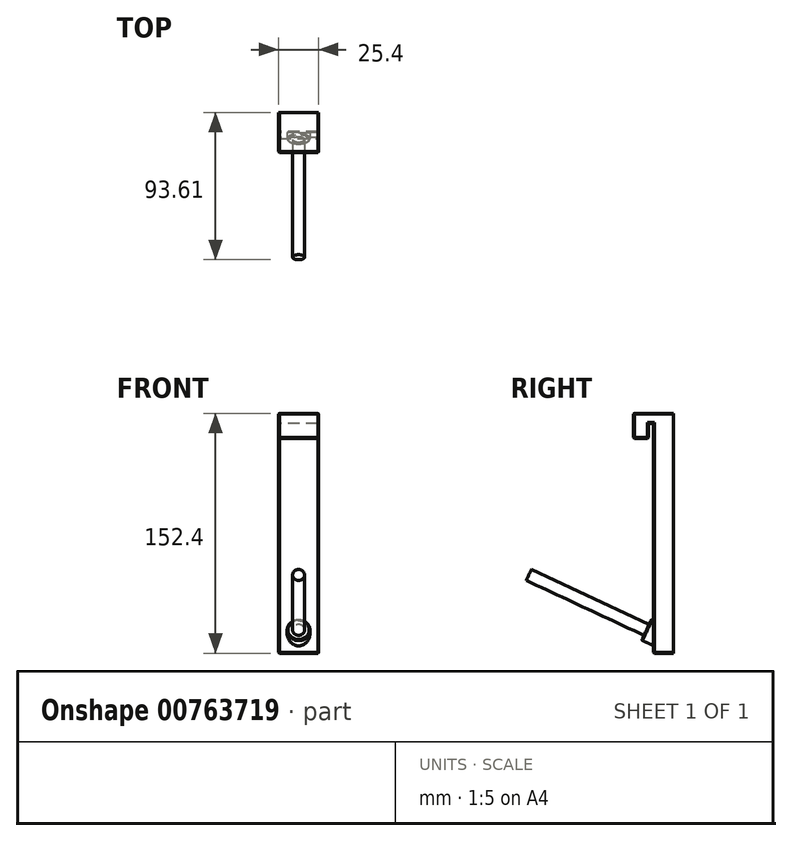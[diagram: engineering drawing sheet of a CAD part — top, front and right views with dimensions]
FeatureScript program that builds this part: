
annotation { "Feature Type Name" : "Feature", "Feature Type Description" : "" }
export const myFeature = defineFeature(function(context is Context, id is Id, definition is map)
    precondition{}
    {
        {
            var Q0;
            Q0=qCreatedBy(makeId("Right.planeOp"),FACE);
            var sketch = newSketch(context, id + "F0", { "sketchPlane" : qUnion([Q0])});
            skLineSegment(sketch, "E0.bottom", {"start": v(-12.7, 76.2) * mm, "end": v(12.7, 76.2) * mm});
            skLineSegment(sketch, "E0.top", {"start": v(-12.7, -76.2) * mm, "end": v(12.7, -76.2) * mm, "construction": true});
            skLineSegment(sketch, "E0.left", {"start": v(-12.7, 76.2) * mm, "end": v(-12.7, -76.2) * mm, "construction": true});
            skLineSegment(sketch, "E0.right", {"start": v(12.7, 76.2) * mm, "end": v(12.7, -76.2) * mm});
            skPoint(sketch, "E0.middle", {"position": v(0, 0) * mm});
            skLineSegment(sketch, "E1", {"start": v(-12.7, 76.2) * mm, "end": v(-12.7, 60.33) * mm});
            skLineSegment(sketch, "E2", {"start": v(-12.7, 60.33) * mm, "end": v(-3.3, 60.33) * mm});
            skLineSegment(sketch, "E3", {"start": v(-3.3, 60.33) * mm, "end": v(-3.3, 69.85) * mm});
            skLineSegment(sketch, "E4", {"start": v(-3.3, 69.85) * mm, "end": v(0, 69.85) * mm});
            skLineSegment(sketch, "E5", {"start": v(0, 69.85) * mm, "end": v(0, -76.2) * mm});
            skLineSegment(sketch, "E6", {"start": v(0, -76.2) * mm, "end": v(12.7, -76.2) * mm});
            skSolve(sketch);
        }
        {
            var Q0;
            Q0 = qSketchRegion(id + "F0", true);
            extrude(context, id + "F1", {"entities" : qUnion([Q0]), "endBound" : BoundingType.SYMMETRIC, "depth" : 25.4 * mm, "offsetDistance" : 25.4 * mm});
        }
        {
            var Q0;
            Q0=qCreatedBy(makeId("Right.planeOp"),FACE);
            var sketch = newSketch(context, id + "F2", { "sketchPlane" : qUnion([Q0])});
            skLineSegment(sketch, "E7", {"start": v(-79.3, -63.5) * mm, "end": v(-79.3, -26.52) * mm, "construction": true});
            skLineSegment(sketch, "E8", {"start": v(12.7, -63.5) * mm, "end": v(-79.3, -63.5) * mm, "construction": true});
            skLineSegment(sketch, "E9", {"start": v(0, 0) * mm, "end": v(0, -63.5) * mm, "construction": true});
            skLineSegment(sketch, "E10", {"start": v(-79.3, -26.52) * mm, "end": v(0, -63.5) * mm, "construction": true});
            skLineSegment(sketch, "E11", {"start": v(-79.3, -26.52) * mm, "end": v(-77.7, -23.07) * mm});
            skLineSegment(sketch, "E12", {"start": v(6.35, -66.46) * mm, "end": v(7.96, -63) * mm});
            skLineSegment(sketch, "E13", {"start": v(7.96, -63) * mm, "end": v(-77.7, -23.07) * mm});
            skLineSegment(sketch, "E14", {"start": v(-79.3, -26.52) * mm, "end": v(6.35, -66.46) * mm});
            skLineSegment(sketch, "E15", {"start": v(0, -59.3) * mm, "end": v(-1.61, -62.75) * mm, "construction": true});
            skLineSegment(sketch, "E16", {"start": v(0, -63.5) * mm, "end": v(12.7, -69.42) * mm, "construction": true});
            skSolve(sketch);
        }
        {
            var Q0;
            Q0 = qSketchRegion(id + "F2", true);
            var Q1;
            Q1=sQuery(id+"F2.wireOp",EDGE,"E14");
            revolve(context, id + "F3", {"operationType" : NewBodyOperationType.ADD, "surfaceOperationType" : NewSurfaceOperationType.NEW, "entities" : qUnion([Q0]), "axis" : qUnion([Q1]), "revolveType" : RevolveType.FULL});
        }
        {
            var Q0;
            Q0=makeQuery(id+"F1.opExtrude","CAP_EDGE",EDGE,{"disambiguationData":[OSD([sQuery(id+"F0.wireOp",EDGE,"E0.bottom")])],"isStart":true});
            var Q1;
            Q1=makeQuery(id+"F1.opExtrude","CAP_EDGE",EDGE,{"disambiguationData":[OSD([sQuery(id+"F0.wireOp",EDGE,"E5")])],"isStart":true});
            var Q2;
            Q2=makeQuery(id+"F1.opExtrude","CAP_EDGE",EDGE,{"disambiguationData":[OSD([sQuery(id+"F0.wireOp",EDGE,"E6")])],"isStart":true});
            var Q3;
            Q3=makeQuery(id+"F1.opExtrude","CAP_EDGE",EDGE,{"disambiguationData":[OSD([sQuery(id+"F0.wireOp",EDGE,"E4")])],"isStart":true});
            var Q4;
            Q4=makeQuery(id+"F1.opExtrude","CAP_EDGE",EDGE,{"disambiguationData":[OSD([sQuery(id+"F0.wireOp",EDGE,"E3")])],"isStart":true});
            var Q5;
            Q5=makeQuery(id+"F1.opExtrude","CAP_EDGE",EDGE,{"disambiguationData":[OSD([sQuery(id+"F0.wireOp",EDGE,"E1")])],"isStart":true});
            var Q6;
            Q6=makeQuery(id+"F1.opExtrude","CAP_EDGE",EDGE,{"disambiguationData":[OSD([sQuery(id+"F0.wireOp",EDGE,"E2")])],"isStart":true});
            var Q7;
            Q7=makeQuery(id+"F1.opExtrude","CAP_EDGE",EDGE,{"disambiguationData":[OSD([sQuery(id+"F0.wireOp",EDGE,"E6")])],"isStart":false});
            var Q8;
            Q8=makeQuery(id+"F1.opExtrude","CAP_EDGE",EDGE,{"disambiguationData":[OSD([sQuery(id+"F0.wireOp",EDGE,"E0.bottom")])],"isStart":false});
            var Q9;
            Q9=makeQuery(id+"F1.opExtrude","CAP_EDGE",EDGE,{"disambiguationData":[OSD([sQuery(id+"F0.wireOp",EDGE,"E1")])],"isStart":false});
            var Q10;
            Q10=makeQuery(id+"F1.opExtrude","CAP_EDGE",EDGE,{"disambiguationData":[OSD([sQuery(id+"F0.wireOp",EDGE,"E4")])],"isStart":false});
            var Q11;
            Q11=makeQuery(id+"F1.opExtrude","CAP_EDGE",EDGE,{"disambiguationData":[OSD([sQuery(id+"F0.wireOp",EDGE,"E3")])],"isStart":false});
            var Q12;
            Q12=makeQuery(id+"F1.opExtrude","CAP_EDGE",EDGE,{"disambiguationData":[OSD([sQuery(id+"F0.wireOp",EDGE,"E2")])],"isStart":false});
            var Q13;
            Q13=makeQuery(id+"F1.opExtrude","CAP_EDGE",EDGE,{"disambiguationData":[OSD([sQuery(id+"F0.wireOp",EDGE,"E5")])],"isStart":false});
            var Q14;
            Q14=makeQuery(id+"F1.opExtrude","SWEPT_EDGE",EDGE,{"disambiguationData":[OSD([sQuery(id+"F0.wireOp",EDGE,"E5"),sQuery(id+"F0.wireOp",EDGE,"E6")])]});
            var Q15;
            Q15=makeQuery(id+"F1.opExtrude","SWEPT_FACE",FACE,{"disambiguationData":[OSD([sQuery(id+"F0.wireOp",EDGE,"E1")])]});
            var Q16;
            Q16=makeQuery(id+"F3.opRevolve","SWEPT_EDGE",EDGE,{"disambiguationData":[OSD([sQuery(id+"F2.wireOp",EDGE,"89eZwPvB-KZEn-1skk-PHsF-nnF3wtStW0cx"),sQuery(id+"F2.wireOp",EDGE,"sWPM6zYz-QN3X-BwLY-xtRB-lTcpQrkUvu8q")])]});
            var Q17;
            Q17=makeQuery(id+"F1.opExtrude","SWEPT_EDGE",EDGE,{"disambiguationData":[OSD([sQuery(id+"F0.wireOp",EDGE,"E2"),sQuery(id+"F0.wireOp",EDGE,"E3")])]});
            chamfer(context, id + "F4", {"entities" : qUnion([Q0, Q1, Q2, Q3, Q4, Q5, Q6, Q7, Q8, Q9, Q10, Q11, Q12, Q13, Q14, Q15, Q16, Q17]), "width" : .5 * mm, "tangentPropagation" : true});
        }
        {
            var Q0;
            Q0=makeQuery(id+"F3.opRevolve","SWEPT_FACE",FACE,{"disambiguationData":[OSD([sQuery(id+"F2.wireOp",EDGE,"E11")])]});
            cPlane(context, id + "F5", {"entities" : qUnion([Q0]), "cplaneType" : CPlaneType.OFFSET, "offset" : 82.55 * mm, "oppositeDirection" : true, "width" : 152.4 * mm, "height" : 152.4 * mm});
        }
        {
            var Q0;
            Q0=qCreatedBy(id+"F5.planeOp",FACE);
            var sketch = newSketch(context, id + "F6", { "sketchPlane" : qUnion([Q0])});
            skCircle(sketch, "E17", {"center": v(0, -57.55) * mm, "radius": 7.25 * mm});
            skLineSegment(sketch, "E18", {"start": v(0, -57.55) * mm, "end": v(-3.8, -57.55) * mm, "construction": true});
            skLineSegment(sketch, "E19", {"start": v(0, -57.55) * mm, "end": v(7.25, -57.55) * mm, "construction": true});
            skSolve(sketch);
        }
        {
            var Q0;
            Q0 = qSketchRegion(id + "F6", true);
            var Q1;
            Q1=makeQuery(id+"F1.opExtrude","SWEPT_FACE",FACE,{"disambiguationData":[OSD([sQuery(id+"F0.wireOp",EDGE,"E5")])]});
            extrude(context, id + "F7", {"entities" : qUnion([Q0]), "operationType" : NewBodyOperationType.ADD, "endBound" : BoundingType.UP_TO_SURFACE, "oppositeDirection" : true, "depth" : 25.4 * mm, "endBoundEntityFace" : qUnion([Q1]), "offsetDistance" : 25.4 * mm});
        }
        {
            var Q0;
            Q0=makeQuery(id+"F7.opExtrude","CAP_EDGE",EDGE,{"disambiguationData":[OSD([sQuery(id+"F6.wireOp",EDGE,"E17")])],"isStart":true});
            chamfer(context, id + "F8", {"entities" : qUnion([Q0]), "width" : .5 * mm, "tangentPropagation" : true});
        }
    });
